FREECAD ASSEMBLY — COMPONENT RECIPES ("assembly_01")

This assembly document has 3 components, labeled P0..P2 below (a component is one placed body or linked part). 0 of them carry a construction recipe — the FreeCAD feature program that regenerates the part from scratch, quoted from this document or its linked companion documents; the rest are supplied as boundary geometry only. No exploded tour is included for this assembly.
COMPONENT P0 — geometry summary ("Body"; no construction recipe available for this part):
  bounding box: 80.0 x 60.0 x 24.0 mm
  tessellated surface: 190,652 triangles
  volume: 23269 mm^3 (20% of its bounding box)
COMPONENT P1 — geometry summary ("Body001"; no construction recipe available for this part):
  bounding box: 80.0 x 60.0 x 4.5 mm
  tessellated surface: 8,100 triangles
  volume: 6221 mm^3 (29% of its bounding box)
COMPONENT P2 — geometry summary ("Body002"; no construction recipe available for this part):
  bounding box: 77.6 x 53.2 x 20.7 mm
  tessellated surface: 166,732 triangles
  volume: 27311 mm^3 (32% of its bounding box)
PROVENANCE & LICENSES
A FreeCAD (.FCStd) document from a public repository crawl; recipes are the document's own serialized feature recipes (and, for linked parts, companion documents' recipes).
License: as declared in the source repository (recorded in the dataset sidecar).
